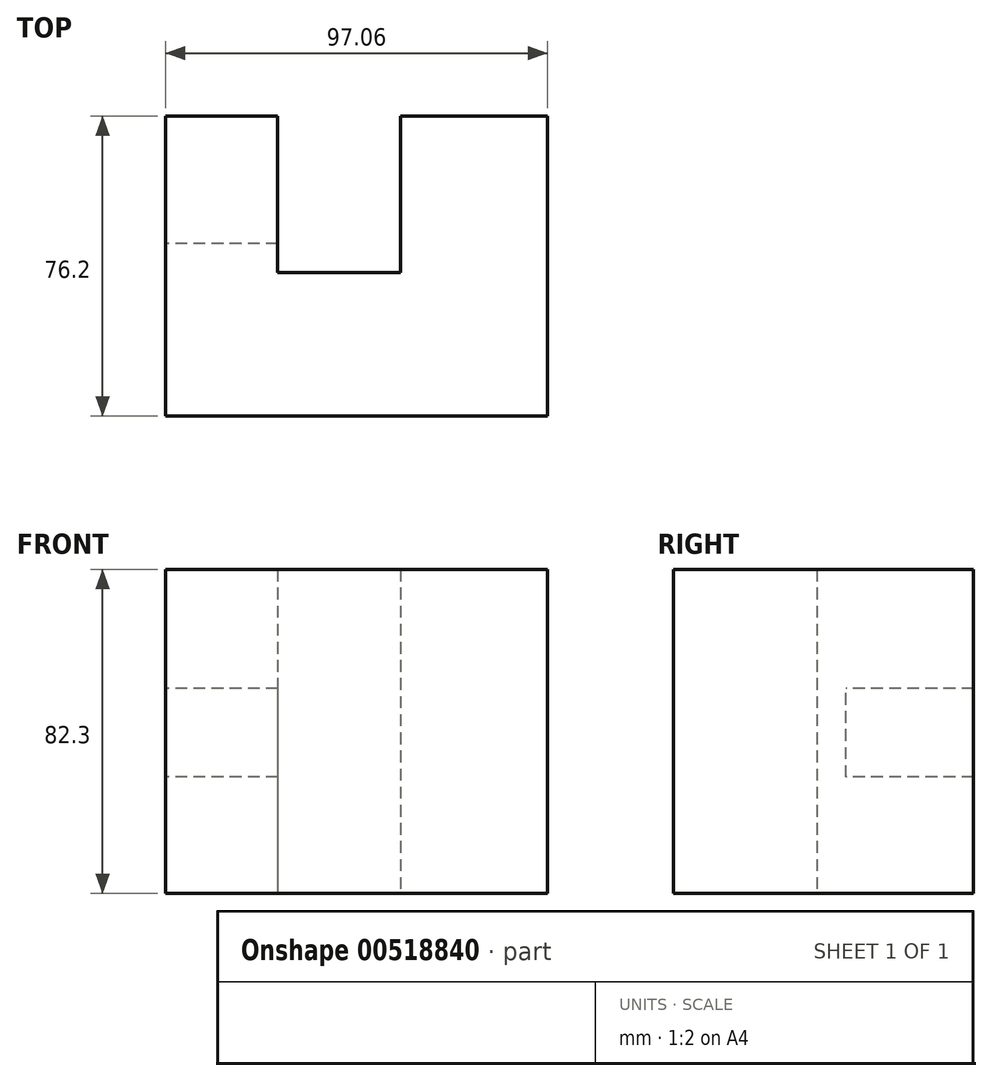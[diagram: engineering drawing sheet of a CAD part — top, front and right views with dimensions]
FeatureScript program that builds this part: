
annotation { "Feature Type Name" : "Feature", "Feature Type Description" : "" }
export const myFeature = defineFeature(function(context is Context, id is Id, definition is map)
    precondition{}
    {
        {
            var Q0;
            Q0=qCreatedBy(makeId("Top.planeOp"),FACE);
            var sketch = newSketch(context, id + "F0", { "sketchPlane" : qUnion([Q0])});
            skLineSegment(sketch, "E0.bottom", {"start": v(-59.66, 39.77) * mm, "end": v(-31.15, 39.77) * mm});
            skLineSegment(sketch, "E0.top", {"start": v(-59.66, -36.43) * mm, "end": v(37.4, -36.43) * mm});
            skLineSegment(sketch, "E0.left", {"start": v(-59.66, 39.77) * mm, "end": v(-59.66, -36.43) * mm});
            skLineSegment(sketch, "E0.right", {"start": v(37.4, 39.77) * mm, "end": v(37.4, -36.43) * mm});
            skLineSegment(sketch, "E1.top", {"start": v(-31.15, 0) * mm, "end": v(0, 0) * mm});
            skLineSegment(sketch, "E1.left", {"start": v(-31.15, 39.77) * mm, "end": v(-31.15, 0) * mm});
            skLineSegment(sketch, "E1.right", {"start": v(0, 39.77) * mm, "end": v(0, 0) * mm});
            skLineSegment(sketch, "E2.trimOffspring", {"start": v(0, 39.77) * mm, "end": v(37.4, 39.77) * mm});
            skSolve(sketch);
        }
        {
            var Q0;
            Q0 = qSketchRegion(id + "F0", true);
            extrude(context, id + "F1", {"entities" : qUnion([Q0]), "depth" : 82.3 * mm});
        }
        {
            var Q0;
            Q0=makeQuery(id+"F1.opExtrude","SWEPT_FACE",FACE,{"disambiguationData":[OSD([sQuery(id+"F0.wireOp",EDGE,"E0.left")])]});
            var sketch = newSketch(context, id + "F2", { "sketchPlane" : qUnion([Q0])});
            skLineSegment(sketch, "E3.bottom", {"start": v(-39.77, 29.55) * mm, "end": v(-7.4, 29.55) * mm});
            skLineSegment(sketch, "E3.top", {"start": v(-39.77, 52.09) * mm, "end": v(-7.4, 52.09) * mm});
            skLineSegment(sketch, "E3.left", {"start": v(-39.77, 29.55) * mm, "end": v(-39.77, 52.09) * mm});
            skLineSegment(sketch, "E3.right", {"start": v(-7.4, 29.55) * mm, "end": v(-7.4, 52.09) * mm});
            skSolve(sketch);
        }
        {
            var Q0;
            Q0 = qSketchRegion(id + "F2", true);
            extrude(context, id + "F3", {"entities" : qUnion([Q0]), "operationType" : NewBodyOperationType.REMOVE, "oppositeDirection" : true, "depth" : 38.35 * mm});
        }
    });
